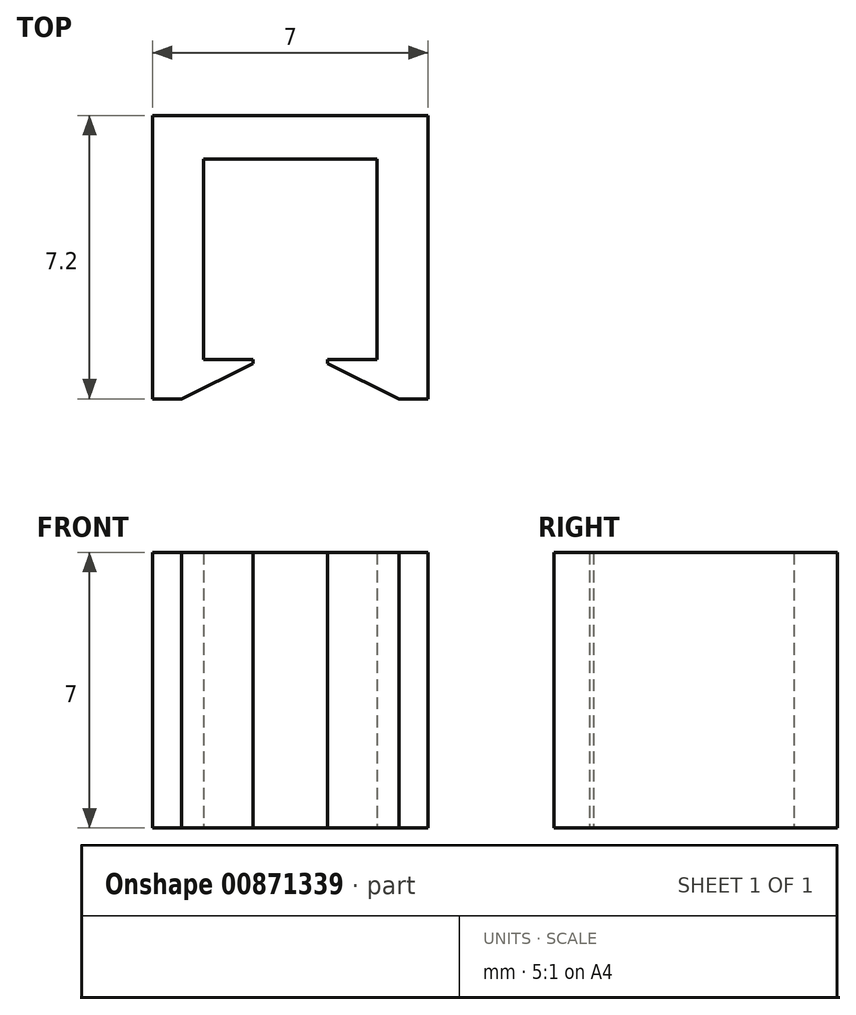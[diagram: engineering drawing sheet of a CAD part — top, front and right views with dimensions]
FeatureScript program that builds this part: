
annotation { "Feature Type Name" : "Feature", "Feature Type Description" : "" }
export const myFeature = defineFeature(function(context is Context, id is Id, definition is map)
    precondition{}
    {
        {
            var Q0;
            Q0=qCreatedBy(makeId("Top.planeOp"),FACE);
            var sketch = newSketch(context, id + "F0", { "sketchPlane" : qUnion([Q0])});
            skLineSegment(sketch, "E0", {"start": v(-2.2, -6.2) * mm, "end": v(-0.95, -6.2) * mm});
            skLineSegment(sketch, "E1", {"start": v(-0.95, -6.2) * mm, "end": v(-0.95, -6.3) * mm});
            skLineSegment(sketch, "E2", {"start": v(-2.76, -7.2) * mm, "end": v(-0.95, -6.3) * mm});
            skLineSegment(sketch, "E3", {"start": v(-2.76, -7.2) * mm, "end": v(-3.5, -7.2) * mm});
            skLineSegment(sketch, "E4", {"start": v(-3.5, -7.2) * mm, "end": v(-3.5, 0) * mm});
            skLineSegment(sketch, "E5", {"start": v(-3.5, 0) * mm, "end": v(3.5, 0) * mm});
            skLineSegment(sketch, "E6", {"start": v(3.5, 0) * mm, "end": v(3.5, -7.2) * mm});
            skLineSegment(sketch, "E7", {"start": v(3.5, -7.2) * mm, "end": v(2.76, -7.2) * mm});
            skLineSegment(sketch, "E8", {"start": v(0.95, -6.3) * mm, "end": v(2.76, -7.2) * mm});
            skLineSegment(sketch, "E9", {"start": v(0.95, -6.3) * mm, "end": v(0.95, -6.2) * mm});
            skLineSegment(sketch, "E10", {"start": v(0.95, -6.2) * mm, "end": v(2.2, -6.2) * mm});
            skLineSegment(sketch, "E11", {"start": v(2.2, -6.2) * mm, "end": v(2.2, -1.1) * mm});
            skLineSegment(sketch, "E12", {"start": v(2.2, -1.1) * mm, "end": v(-2.2, -1.1) * mm});
            skLineSegment(sketch, "E13", {"start": v(-2.2, -1.1) * mm, "end": v(-2.2, -6.2) * mm});
            skSolve(sketch);
        }
        {
            var Q0;
            Q0=makeQuery(id+"F0.imprint","IMPRINT",FACE,{"disambiguationData":[TD([[makeQuery(id+"F0.imprint","IMPRINT",EDGE,{"derivedFrom":sQuery(id+"F0.wireOp",EDGE,"E0")}),-1.0]])]});
            extrude(context, id + "F1", {"entities" : qUnion([Q0]), "depth" : 7 * mm, "offsetDistance" : 25 * mm});
        }
    });
